# Revit family: Plumbing_Drainage_Menzies-Metal_Clamp-Tite_Overflow-Scupper-Drain_TPO
name_source: partatom
category: Plumbing Fixtures
revit_build: Autodesk Revit 2018 (Build: 20170223_1515(x64)
units: mm (PartAtom-declared; Revit-internal decimal feet)

## family parameters
Cut with Voids When Loaded = No
Host = Face
OmniClass Number = 23.70.50.21.24.11
OmniClass Title = Roof Waste Water Drains
Part Type = Normal
Room Calculation Point = No
Round Connector Dimension = Use Diameter
Shared = No

## types (1)
- 3"
    Assembly Code = D2040200
    Default Elevation = 48 "
    Description = Clamp-Tite Overflow Scupper Drain TPO
    Drain Flow = 0 GPM
    Edition number = 1
    Manufacturer = Menzies Metal Products
    Model = 300-3170TPO
    Pipe Diameter = 3"
    Pipe Length = 11 "
    Pipe Length Note = Longer pipes available.  Pipes can be field cut to the desired length.
    Product Guid = ea79d50d-b752-4271-8b4b-809d51799292
    Product Material = Metal - Menzies Metal Products - Copper
    Product data url = https://www.bimobject.com
    URL = https://www.menzies-metal.com
    Weight = 2.10 lbf

## geometry (parser evidence)
native form markers: Sweep x2
no freeform markers — native parametric forms only
